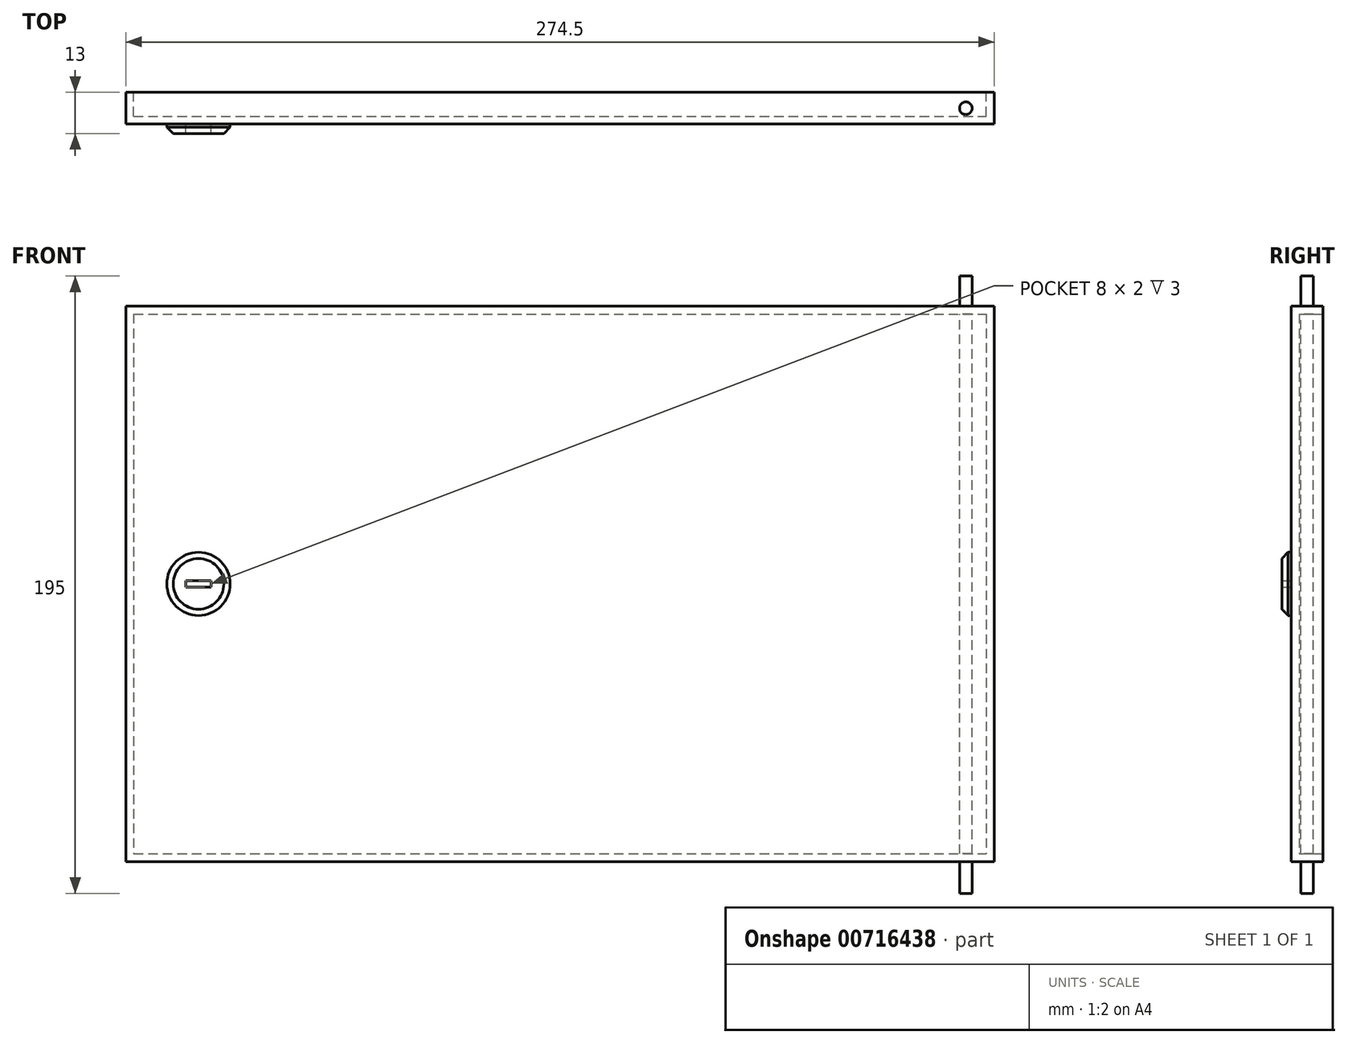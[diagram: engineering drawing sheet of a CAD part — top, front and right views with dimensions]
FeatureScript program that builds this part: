
annotation { "Feature Type Name" : "Feature", "Feature Type Description" : "" }
export const myFeature = defineFeature(function(context is Context, id is Id, definition is map)
    precondition{}
    {
        {
            var Q0;
            Q0=qCreatedBy(makeId("Top.planeOp"),FACE);
            var sketch = newSketch(context, id + "F0", { "sketchPlane" : qUnion([Q0])});
            skLineSegment(sketch, "E0.bottom", {"start": v(0, 0) * mm, "end": v(274.5, 0) * mm});
            skLineSegment(sketch, "E0.top", {"start": v(0, 10) * mm, "end": v(274.5, 10) * mm});
            skLineSegment(sketch, "E0.left", {"start": v(0, 0) * mm, "end": v(0, 10) * mm});
            skLineSegment(sketch, "E0.right", {"start": v(274.5, 0) * mm, "end": v(274.5, 10) * mm});
            skSolve(sketch);
        }
        {
            var Q0;
            Q0=qSketchRegion(id+"F0",true);
            extrude(context, id + "F1", {"entities" : qUnion([Q0]), "depth" : 175.5 * mm, "offsetDistance" : 25 * mm});
        }
        {
            var Q0;
            Q0=makeQuery(id+"F1.opExtrude","SWEPT_FACE",FACE,{"disambiguationData":[OSD([sQuery(id+"F0.wireOp",EDGE,"E0.top")])]});
            shell(context, id + "F2", {"entities" : qUnion([Q0]), "thickness" : 2.5 * mm});
        }
        {
            var Q0;
            Q0=makeQuery(id+"F1.opExtrude","CAP_FACE",FACE,{"disambiguationData":[OSD([sQuery(id+"F0.wireOp",EDGE,"E0.bottom"),sQuery(id+"F0.wireOp",EDGE,"E0.top"),sQuery(id+"F0.wireOp",EDGE,"E0.left"),sQuery(id+"F0.wireOp",EDGE,"E0.right")])],"isStart":true});
            var sketch = newSketch(context, id + "F3", { "sketchPlane" : qUnion([Q0])});
            skCircle(sketch, "E1", {"center": v(265.5, -5) * mm, "radius": 2 * mm});
            skPoint(sketch, "E1.centerSnap0", {"position": v(274.5, -5) * mm});
            skSolve(sketch);
        }
        {
            var Q0;
            Q0=qSketchRegion(id+"F3",true);
            extrude(context, id + "F4", {"entities" : qUnion([Q0]), "operationType" : NewBodyOperationType.ADD, "depth" : 10 * mm, "offsetDistance" : 25 * mm, "hasSecondDirection" : true, "secondDirectionOppositeDirection" : true, "secondDirectionDepth" : 185 * mm});
        }
        {
            var Q0;
            Q0=makeQuery(id+"F1.opExtrude","SWEPT_FACE",FACE,{"disambiguationData":[OSD([sQuery(id+"F0.wireOp",EDGE,"E0.bottom")])]});
            var sketch = newSketch(context, id + "F5", { "sketchPlane" : qUnion([Q0])});
            skCircle(sketch, "E2", {"center": v(22.98, 87.75) * mm, "radius": 10 * mm});
            skPoint(sketch, "E2.centerSnap0", {"position": v(0, 87.75) * mm});
            skLineSegment(sketch, "E3.bottom", {"start": v(18.98, 88.75) * mm, "end": v(26.98, 88.75) * mm});
            skLineSegment(sketch, "E3.top", {"start": v(18.98, 86.75) * mm, "end": v(26.98, 86.75) * mm});
            skLineSegment(sketch, "E3.left", {"start": v(18.98, 88.75) * mm, "end": v(18.98, 86.75) * mm});
            skLineSegment(sketch, "E3.right", {"start": v(26.98, 88.75) * mm, "end": v(26.98, 86.75) * mm});
            skSolve(sketch);
        }
        {
            var Q0;
            Q0 = qSketchRegion(id + "F5", true);
            extrude(context, id + "F6", {"entities" : qUnion([Q0]), "operationType" : NewBodyOperationType.ADD, "depth" : 3 * mm, "offsetDistance" : 25 * mm});
        }
        {
            var Q0;
            Q0=makeQuery(id+"F6.opExtrude","CAP_EDGE",EDGE,{"disambiguationData":[OSD([sQuery(id+"F5.wireOp",EDGE,"E2")])],"isStart":false});
            chamfer(context, id + "F7", {"entities" : qUnion([Q0]), "width" : 2 * mm, "tangentPropagation" : true});
        }
    });
